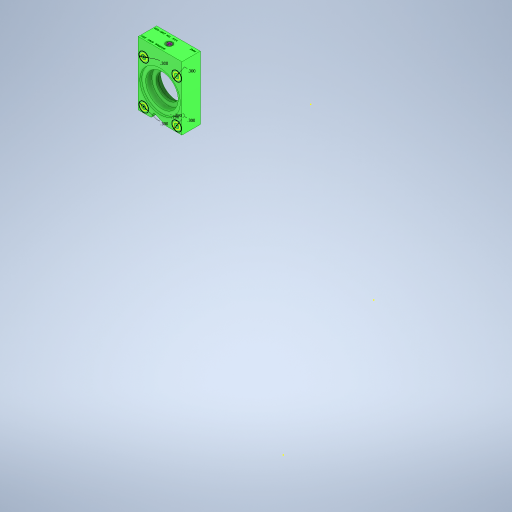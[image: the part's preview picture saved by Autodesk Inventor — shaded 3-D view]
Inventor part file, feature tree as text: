
AUTODESK INVENTOR PART (.ipt)
format: ipt  version: 2024.1 (Build 281209000, 209)  size: 720,896 bytes
history: native  units: in
note: dims shown in document units (in); Inventor stores cm internally (conversion verified against a paired STEP export)
features: hole x8, extrude x5, sketch x4, fillet x1
ambient origin geometry x8: Origin, YZ Plane, XZ Plane, XY Plane, X Axis, Y Axis, Z Axis, Center Point
bodies: Solid1 (feature_tree)
feature tree (18):
  extrude  "Extrusion1"  Depth=0.4in TaperAngle=0.0deg
  extrude  "Extrusion2"  Depth=0.375in
  extrude  "Extrusion3"  Depth=0.375in
  hole  "Hole1"  [1 undecoded]
  hole  "Hole2"  [1 undecoded]
  extrude  "Extrusion4"  Depth=0.375in
  hole  "Hole5"  [1 undecoded]
  hole  "Hole6"  [1 undecoded]
  fillet  "Fillet1"  Radius=1.0in
  sketch  "Sketch7"  dims[d13=0.06in d14=0.75in d15=0.507in d16=0.25in d17=0.5635in d18=1.0in d19=0.8108in d20=0.4583in d21=0.29in d22=0.04in d23=0.75in d24=0.507in d25=0.25in d26=0.5635in d27=1.0in d28=0.8108in d29=0.213in d30=0.75in d31=0.507in d32=0.25in d33=0.5635in d34=0.25in d35=0.0in d36=0.75in d38=135.0deg d39=0.4583in d40=112.5deg d41=0.25in d42=1.0in d43=0.0in d44=0.29in d45=0.196in d46=0.211in d47=0.25in d48=0.375in d49=0.25in d50=0.5635in d51=0.25in d52=0.0in d53=0.06in d54=0.75in d55=0.375in d56=0.25in d57=0.5635in d58=0.6in d59=0.8108in d60=0.0312in d61=0.13in d62=0.6in d63=0.375in d64=0.25in d65=0.5635in d66=0.484in d67=0.0in d68=0.5in d69=0.0in d70=0.3in d71=0.3in d72=0.3in d73=0.3in d74=0.136in d75=0.75in d76=0.375in d77=0.19in d78=0.5635in d79=1.0in d80=0.8108in]
  extrude  "Extrusion5"  Depth=0.375in
  hole  "Hole7"  [1 undecoded]
  hole  "Hole8"  [1 undecoded]
  hole  "Hole3"  [1 undecoded]
  hole  "Hole4"  [1 undecoded]
  sketch  "Sketch1"  dims[d0=0.5in d1=0.0in d2=0.4in d3=0.0in]
  sketch  "Sketch2"  dims[d4=0.6in d5=0.0in]
  sketch  "Sketch5"  dims[d6=0.211in d7=0.25in d8=0.507in d9=0.25in d10=0.5635in d11=0.25in d12=0.0in]
note: 8 required parameter values undecoded (feature->parameter linkage not recoverable at this tier; creation-order binding heuristic only, values carry confidence <= 0.55)
